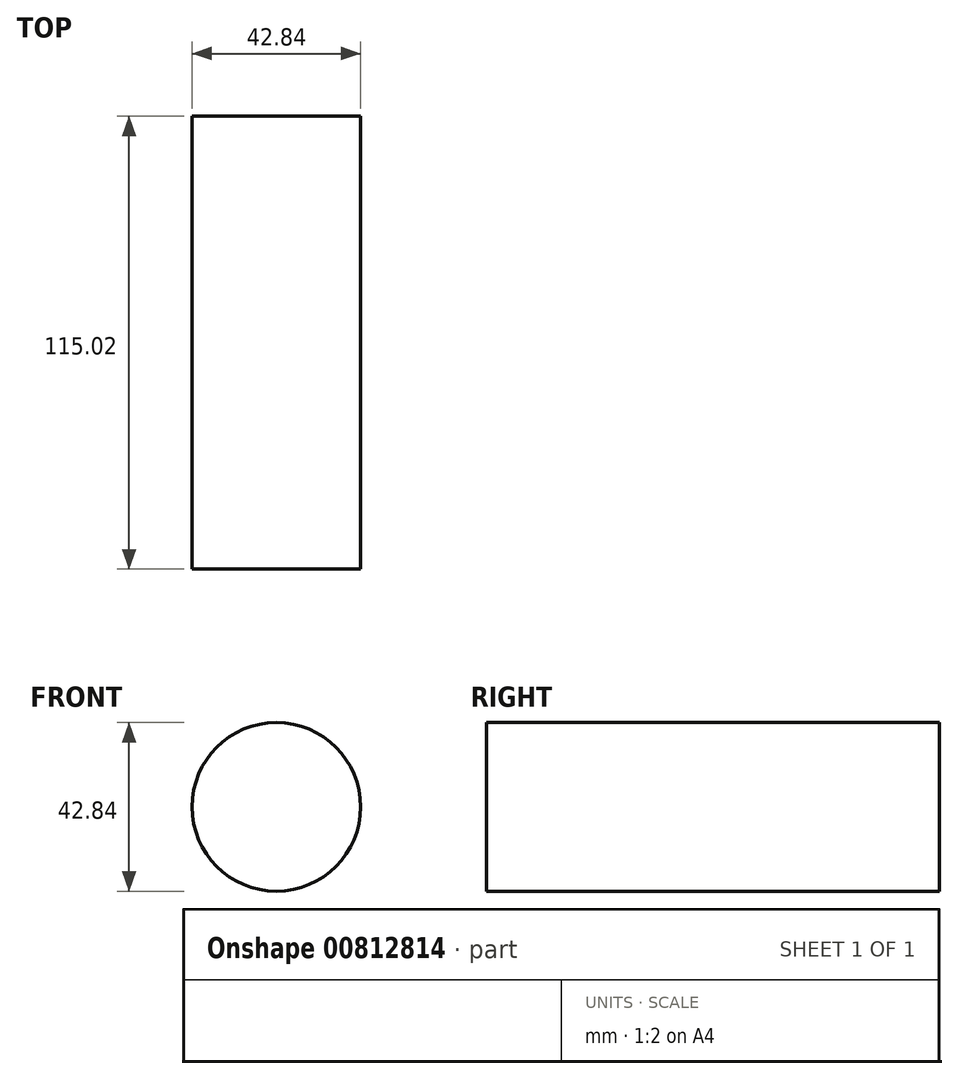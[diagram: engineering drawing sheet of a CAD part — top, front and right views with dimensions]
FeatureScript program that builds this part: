
annotation { "Feature Type Name" : "Feature", "Feature Type Description" : "" }
export const myFeature = defineFeature(function(context is Context, id is Id, definition is map)
    precondition{}
    {
        {
            var Q0;
            Q0=qCreatedBy(makeId("Front.planeOp"),FACE);
            var sketch = newSketch(context, id + "F0", { "sketchPlane" : qUnion([Q0])});
            skCircle(sketch, "E0", {"center": v(-55.64, 0) * mm, "radius": 21.42 * mm});
            skSolve(sketch);
        }
        {
            var Q0;
            Q0 = qSketchRegion(id + "F0", true);
            extrude(context, id + "F1", {"entities" : qUnion([Q0]), "depth" : 115.02 * mm, "offsetDistance" : 25 * mm});
        }
    });
